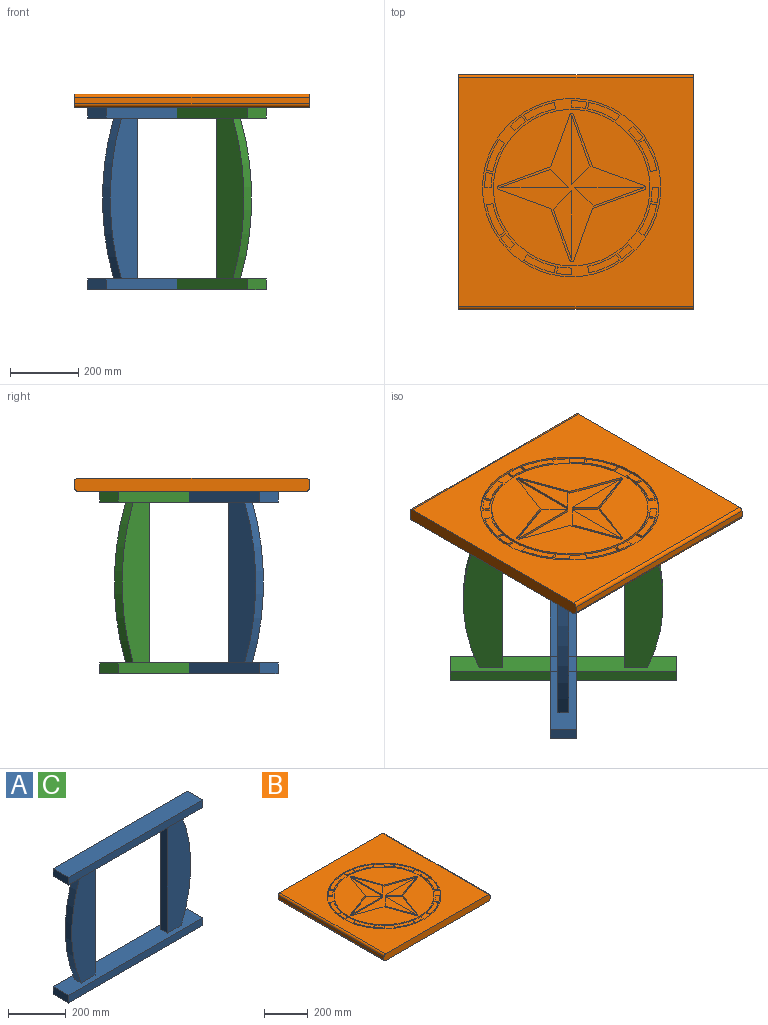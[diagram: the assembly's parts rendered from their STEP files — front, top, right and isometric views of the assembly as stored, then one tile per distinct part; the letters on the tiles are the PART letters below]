
ASSEMBLY  parts=3 mates=1
PART A: 20 faces, bbox 660.4x76.2x533.4 mm
  f0: plane 469.9x114.3mm, normal (0,-1,0), area 46605.8mm2, adj f4,f7,f8,f13
  f1: plane 469.9x114.3mm, normal (0,-1,0), area 46605.8mm2, adj f5,f8,f12,f13
  f2: plane 469.9x114.3mm, normal (0,1,0), area 46605.8mm2, adj f4,f7,f8,f13
  f3: plane 469.9x114.3mm, normal (0,1,0), area 46605.8mm2, adj f5,f8,f12,f13
  f4: plane 469.9x31.75mm, normal (1,0,0), area 14919.3mm2, adj f0,f2,f8,f13
  f5: plane 469.9x31.75mm, normal (-1,0,0), area 14919.3mm2, adj f1,f3,f8,f13
  f6: plane 76.2x31.75mm, normal (-1,0,0), area 2419.3mm2, adj f13,f15,f16,f17
  f7: cylinder r=622.3mm len=469.9mm, axis (0,1,0), area 15298.6mm2, adj f0,f2,f8,f13
  f8: plane 660.4x76.2mm, normal (0,0,1), area 45989.1mm2, adj f0,f1,f2,f3,f4,f5,f7,f9
  f9: plane 76.2x31.75mm, normal (-1,0,0), area 2419.3mm2, adj f8,f10,f18,f19
  f10: plane 660.4x76.2mm, normal (0,0,-1), area 50322.5mm2, adj f9,f11,f18,f19
  f11: plane 76.2x31.75mm, normal (1,0,0), area 2419.3mm2, adj f8,f10,f18,f19
  f12: cylinder r=622.3mm len=469.9mm, axis (0,1,0), area 15298.6mm2, adj f1,f3,f8,f13
  f13: plane 660.4x76.2mm, normal (0,0,-1), area 45989.1mm2, adj f0,f1,f2,f3,f4,f5,f6,f7
  f14: plane 76.2x31.75mm, normal (1,0,0), area 2419.3mm2, adj f13,f15,f16,f17
  f15: plane 660.4x76.2mm, normal (0,0,1), area 50322.5mm2, adj f6,f14,f16,f17
  f16: plane 660.4x31.75mm, normal (0,1,0), area 20967.7mm2, adj f6,f13,f14,f15
  f17: plane 660.4x31.75mm, normal (0,-1,0), area 20967.7mm2, adj f6,f13,f14,f15
  f18: plane 660.4x31.75mm, normal (0,1,0), area 20967.7mm2, adj f8,f9,f10,f11
  f19: plane 660.4x31.75mm, normal (0,-1,0), area 20967.7mm2, adj f8,f9,f10,f11
PART B: 123 faces, bbox 685.8x685.8x38.1 mm
  f0: plane 457.2x457.2mm, normal (0,0,1), area 108640mm2, adj f76,f96,f97,f98,f99,f100,f101,f102
  f1: plane 685.8x666.75mm, normal (0,0,1), area 244313.3mm2, adj f3,f5,f9,f10,f59
  f2: plane 685.8x19.05mm, normal (-1,0,0), area 13064.5mm2, adj f3,f5,f8,f10
  f3: plane 685.8x38.1mm, normal (0,-1,0), area 26051.1mm2, adj f1,f2,f4,f6,f7,f8,f9,f10
  f4: plane 685.8x19.05mm, normal (1,0,0), area 13064.5mm2, adj f3,f5,f7,f9
  f5: plane 685.8x38.1mm, normal (0,1,0), area 26051.1mm2, adj f1,f2,f4,f6,f7,f8,f9,f10
  f6: plane 685.8x666.75mm, normal (0,0,-1), area 457257.1mm2, adj f3,f5,f7,f8
  f7: cylinder r=9.53mm len=685.8mm, axis (0,1,0), area 10260.8mm2, adj f3,f4,f5,f6
  f8: cylinder r=9.53mm len=685.8mm, axis (0,-1,0), area 10260.8mm2, adj f2,f3,f5,f6
  f9: cylinder r=9.53mm len=685.8mm, axis (0,-1,0), area 10260.8mm2, adj f1,f3,f4,f5
  f10: cylinder r=9.53mm len=685.8mm, axis (0,1,0), area 10260.8mm2, adj f1,f2,f3,f5
  f11: cylinder r=254mm len=90.1mm, axis (0,0,1), area 623.1mm2, adj f12,f60,f77,f93
  f12: plane 18.77x6.35mm, normal (0.17,-0.98,0), area 121mm2, adj f11,f13,f77,f93
  f13: cylinder r=234.95mm len=82.47mm, axis (0,0,1), area 570.3mm2, adj f12,f60,f77,f93
  f14: cylinder r=254mm len=33.92mm, axis (0,0,1), area 281.5mm2, adj f15,f61,f77,f92
  f15: plane 15.61x10.93mm, normal (0.57,-0.82,0), area 121mm2, adj f14,f16,f77,f92
  f16: cylinder r=234.95mm len=31.37mm, axis (0,0,1), area 260.4mm2, adj f15,f61,f77,f92
  f17: cylinder r=254mm len=33.92mm, axis (0,0,1), area 281.5mm2, adj f18,f62,f77,f91
  f18: plane 15.61x10.93mm, normal (0.82,0.57,0), area 121mm2, adj f17,f19,f77,f91
  f19: cylinder r=234.95mm len=31.37mm, axis (0,0,1), area 260.4mm2, adj f18,f62,f77,f91
  f20: cylinder r=254mm len=90.1mm, axis (0,0,1), area 623.1mm2, adj f21,f63,f77,f90
  f21: plane 15.61x10.93mm, normal (0.57,0.82,0), area 121mm2, adj f20,f22,f77,f90
  f22: cylinder r=234.95mm len=82.47mm, axis (0,0,1), area 570.3mm2, adj f21,f63,f77,f90
  f23: cylinder r=254mm len=44.11mm, axis (0,0,1), area 281.5mm2, adj f24,f64,f77,f89
  f24: plane 18.76x6.35mm, normal (0.17,0.98,0), area 121mm2, adj f23,f25,f77,f89
  f25: cylinder r=234.95mm len=40.8mm, axis (0,0,1), area 260.4mm2, adj f24,f64,f77,f89
  f26: cylinder r=254mm len=90.1mm, axis (0,0,1), area 623.1mm2, adj f27,f65,f77,f88
  f27: plane 18.77x6.35mm, normal (-0.17,0.98,0), area 121mm2, adj f26,f28,f77,f88
  f28: cylinder r=234.95mm len=82.47mm, axis (0,0,1), area 570.3mm2, adj f27,f65,f77,f88
  f29: cylinder r=254mm len=33.92mm, axis (0,0,1), area 281.5mm2, adj f30,f66,f77,f87
  f30: plane 15.61x10.93mm, normal (-0.57,0.82,0), area 121mm2, adj f29,f31,f77,f87
  f31: cylinder r=234.95mm len=31.37mm, axis (0,0,1), area 260.4mm2, adj f30,f66,f77,f87
  f32: cylinder r=254mm len=90.1mm, axis (0,0,1), area 623.1mm2, adj f33,f67,f77,f86
  f33: plane 15.61x10.93mm, normal (-0.82,0.57,0), area 121mm2, adj f32,f34,f77,f86
  f34: cylinder r=234.95mm len=82.47mm, axis (0,0,1), area 570.3mm2, adj f33,f67,f77,f86
  f35: cylinder r=254mm len=44.11mm, axis (0,0,1), area 281.5mm2, adj f36,f68,f77,f85
  f36: plane 18.76x6.35mm, normal (-0.98,0.17,0), area 121mm2, adj f35,f37,f77,f85
  f37: cylinder r=234.95mm len=40.8mm, axis (0,0,1), area 260.4mm2, adj f36,f68,f77,f85
  f38: cylinder r=254mm len=90.1mm, axis (0,0,1), area 623.1mm2, adj f39,f69,f77,f84
  f39: plane 18.77x6.35mm, normal (-0.98,-0.17,0), area 121mm2, adj f38,f40,f77,f84
  f40: cylinder r=234.95mm len=82.47mm, axis (0,0,1), area 570.3mm2, adj f39,f69,f77,f84
  f41: cylinder r=254mm len=33.92mm, axis (0,0,1), area 281.5mm2, adj f42,f70,f77,f83
  f42: plane 15.61x10.93mm, normal (-0.82,-0.57,0), area 121mm2, adj f41,f43,f77,f83
  f43: cylinder r=234.95mm len=31.37mm, axis (0,0,1), area 260.4mm2, adj f42,f70,f77,f83
  f44: cylinder r=254mm len=90.1mm, axis (0,0,1), area 623.1mm2, adj f45,f71,f77,f82
  f45: plane 15.61x10.93mm, normal (-0.57,-0.82,0), area 121mm2, adj f44,f46,f77,f82
  f46: cylinder r=234.95mm len=82.47mm, axis (0,0,1), area 570.3mm2, adj f45,f71,f77,f82
  f47: cylinder r=254mm len=44.11mm, axis (0,0,1), area 281.5mm2, adj f48,f72,f77,f81
  f48: plane 18.76x6.35mm, normal (-0.17,-0.98,0), area 121mm2, adj f47,f49,f77,f81
  f49: cylinder r=234.95mm len=40.8mm, axis (0,0,1), area 260.4mm2, adj f48,f72,f77,f81
  f50: cylinder r=234.95mm len=82.47mm, axis (0,0,1), area 570.3mm2, adj f51,f73,f77,f80
  f51: plane 18.77x6.35mm, normal (-0.98,0.17,0), area 121mm2, adj f50,f52,f77,f80
  f52: cylinder r=254mm len=90.1mm, axis (0,0,1), area 623.1mm2, adj f51,f73,f77,f80
  f53: plane 18.77x6.35mm, normal (0.98,0.17,0), area 121mm2, adj f54,f74,f77,f79
  f54: cylinder r=234.95mm len=82.47mm, axis (0,0,1), area 570.3mm2, adj f53,f55,f77,f79
  f55: plane 15.61x10.93mm, normal (-0.82,-0.57,0), area 121mm2, adj f54,f74,f77,f79
  f56: cylinder r=234.95mm len=40.8mm, axis (0,0,1), area 260.4mm2, adj f57,f75,f77,f78
  f57: plane 19.05x6.35mm, normal (-1,0,0), area 121mm2, adj f56,f58,f77,f78
  f58: cylinder r=254mm len=44.11mm, axis (0,0,1), area 281.5mm2, adj f57,f75,f77,f78
  f59: cylinder r=260.35mm len=520.7mm, axis (0,0,1), area 10387.5mm2, adj f1,f77
  f60: plane 15.61x10.93mm, normal (-0.57,0.82,0), area 121mm2, adj f11,f13,f77,f93
  f61: plane 13.47x13.47mm, normal (-0.71,0.71,0), area 121mm2, adj f14,f16,f77,f92
  f62: plane 13.47x13.47mm, normal (-0.71,-0.71,0), area 121mm2, adj f17,f19,f77,f91
  f63: plane 18.77x6.35mm, normal (-0.17,-0.98,0), area 121mm2, adj f20,f22,f77,f90
  f64: plane 19.05x6.35mm, normal (0,-1,0), area 121mm2, adj f23,f25,f77,f89
  f65: plane 15.61x10.93mm, normal (0.57,-0.82,0), area 121mm2, adj f26,f28,f77,f88
  f66: plane 13.47x13.47mm, normal (0.71,-0.71,0), area 121mm2, adj f29,f31,f77,f87
  f67: plane 18.77x6.35mm, normal (0.98,-0.17,0), area 121mm2, adj f32,f34,f77,f86
  f68: plane 19.05x6.35mm, normal (1,0,0), area 121mm2, adj f35,f37,f77,f85
  f69: plane 15.61x10.93mm, normal (0.82,0.57,0), area 121mm2, adj f38,f40,f77,f84
  f70: plane 13.47x13.47mm, normal (0.71,0.71,0), area 121mm2, adj f41,f43,f77,f83
  f71: plane 18.77x6.35mm, normal (0.17,0.98,0), area 121mm2, adj f44,f46,f77,f82
  f72: plane 19.05x6.35mm, normal (0,1,0), area 121mm2, adj f47,f49,f77,f81
  f73: plane 15.61x10.93mm, normal (0.82,-0.57,0), area 121mm2, adj f50,f52,f77,f80
  f74: cylinder r=254mm len=90.1mm, axis (0,0,1), area 623.1mm2, adj f53,f55,f77,f79
  f75: plane 18.76x6.35mm, normal (0.98,-0.17,0), area 121mm2, adj f56,f58,f77,f78
  f76: cylinder r=228.6mm len=457.2mm, axis (0,0,1), area 9120.7mm2, adj f0,f77
  f77: plane 520.7x520.7mm, normal (0,0,1), area 27946.7mm2, adj f11,f12,f13,f14,f15,f16,f17,f18
  f78: plane 44.11x22.62mm, normal (0,0,1), area 812.8mm2, adj f56,f57,f58,f75
  f79: plane 93.4x52.93mm, normal (0,0,1), area 1790.1mm2, adj f53,f54,f55,f74
  f80: plane 93.4x52.93mm, normal (0,0,1), area 1790.1mm2, adj f50,f51,f52,f73
  f81: plane 44.11x22.62mm, normal (0,0,1), area 812.8mm2, adj f47,f48,f49,f72
  f82: plane 93.4x52.93mm, normal (0,0,1), area 1790.1mm2, adj f44,f45,f46,f71
  f83: plane 44.84x41.93mm, normal (0,0,1), area 812.8mm2, adj f41,f42,f43,f70
  f84: plane 93.4x52.93mm, normal (0,0,1), area 1790.1mm2, adj f38,f39,f40,f69
  f85: plane 44.11x22.62mm, normal (0,0,1), area 812.8mm2, adj f35,f36,f37,f68
  f86: plane 93.4x52.93mm, normal (0,0,1), area 1790.1mm2, adj f32,f33,f34,f67
  f87: plane 44.84x41.93mm, normal (0,0,1), area 812.8mm2, adj f29,f30,f31,f66
  f88: plane 93.4x52.93mm, normal (0,0,1), area 1790.1mm2, adj f26,f27,f28,f65
  f89: plane 44.11x22.62mm, normal (0,0,1), area 812.8mm2, adj f23,f24,f25,f64
  f90: plane 93.4x52.93mm, normal (0,0,1), area 1790.1mm2, adj f20,f21,f22,f63
  f91: plane 44.84x41.93mm, normal (0,0,1), area 812.8mm2, adj f17,f18,f19,f62
  f92: plane 44.84x41.93mm, normal (0,0,1), area 812.8mm2, adj f14,f15,f16,f61
  f93: plane 93.4x52.93mm, normal (0,0,1), area 1790.1mm2, adj f11,f12,f13,f60
  f94: plane 147.4x53.65mm, normal (-0.34,0.94,0), area 996.1mm2, adj f95,f114,f115,f116
  f95: plane 53.65x53.65mm, normal (0.71,0.71,0), area 481.8mm2, adj f94,f114,f115,f116
  f96: plane 151.2x55.03mm, normal (-0.34,0.94,0), area 1021.8mm2, adj f0,f97,f112,f116
  f97: cylinder r=6.35mm len=11.93mm, axis (0,0,1), area 98.5mm2, adj f0,f96,f98,f116
  f98: plane 151.2x55.03mm, normal (-0.34,-0.94,0), area 1021.8mm2, adj f0,f97,f99,f116
  f99: plane 151.2x55.03mm, normal (-0.94,-0.34,0), area 1021.8mm2, adj f0,f98,f100,f116
  f100: cylinder r=6.35mm len=11.93mm, axis (0,0,1), area 98.5mm2, adj f0,f99,f101,f116
  f101: plane 151.2x55.03mm, normal (0.94,-0.34,0), area 1021.8mm2, adj f0,f100,f102,f116
  f102: plane 151.2x55.03mm, normal (0.34,-0.94,0), area 1021.8mm2, adj f0,f101,f103,f116
  f103: cylinder r=6.35mm len=11.93mm, axis (0,0,1), area 98.5mm2, adj f0,f102,f104,f116
  f104: plane 151.2x55.03mm, normal (0.34,0.94,0), area 1021.8mm2, adj f0,f103,f105,f116
  f105: plane 151.2x55.03mm, normal (0.94,0.34,0), area 1021.8mm2, adj f0,f104,f106,f116
  f106: cylinder r=6.35mm len=11.93mm, axis (0,0,1), area 98.5mm2, adj f0,f105,f112,f116
  f107: plane 147.4x53.65mm, normal (-0.94,-0.34,0), area 996.1mm2, adj f108,f116,f117,f118
  f108: plane 53.65x53.65mm, normal (-0.71,0.71,0), area 481.8mm2, adj f107,f116,f117,f118
  f109: plane 147.4x53.65mm, normal (0.34,-0.94,0), area 996.1mm2, adj f113,f116,f119,f120
  f110: plane 147.4x53.65mm, normal (0.94,0.34,0), area 996.1mm2, adj f111,f116,f121,f122
  f111: plane 53.65x53.65mm, normal (0.71,-0.71,0), area 481.8mm2, adj f110,f116,f121,f122
  f112: plane 151.2x55.03mm, normal (-0.94,0.34,0), area 1021.8mm2, adj f0,f96,f106,f116
  f113: plane 53.65x53.65mm, normal (-0.71,-0.71,0), area 481.8mm2, adj f109,f116,f119,f120
  f114: plane 201.05x53.65mm, normal (0,0,1), area 5393.3mm2, adj f94,f95,f115
  f115: plane 201.05x6.35mm, normal (0,-1,0), area 1276.7mm2, adj f94,f95,f114,f116
  f116: plane 432.77x432.77mm, normal (0,0,1), area 33960.1mm2, adj f94,f95,f96,f97,f98,f99,f100,f101
  f117: plane 201.05x53.65mm, normal (0,0,1), area 5393.3mm2, adj f107,f108,f118
  f118: plane 201.05x6.35mm, normal (1,0,0), area 1276.7mm2, adj f107,f108,f116,f117
  f119: plane 201.05x53.65mm, normal (0,0,1), area 5393.3mm2, adj f109,f113,f120
  f120: plane 201.05x6.35mm, normal (0,1,0), area 1276.7mm2, adj f109,f113,f116,f119
  f121: plane 201.05x53.65mm, normal (0,0,1), area 5393.3mm2, adj f110,f111,f122
  f122: plane 201.05x6.35mm, normal (-1,0,0), area 1276.7mm2, adj f110,f111,f116,f121
PART C: same geometry as A
PLACE A rot(axis=(0,0,1),45deg) t=(-228.55,69.55,-257.33)mm
PLACE B rot(axis=(0,0,-1),90deg) t=(46.97,295.51,276.07)mm
PLACE C rot(axis=(0,0,-1),45deg) t=(-206.1,536.52,-257.33)mm
MATE fastened C.f15 <-> A.f15  axis (0,0,1) through (16.16,291.81,276.07)mm
